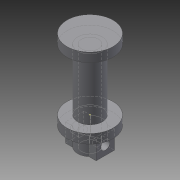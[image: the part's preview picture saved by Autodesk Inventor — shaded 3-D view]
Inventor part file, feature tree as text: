
AUTODESK INVENTOR PART (.ipt)
format: ipt  version: 2015 (Build 190159000, 159)  size: 158,208 bytes
history: native  units: mm
features: sketch x10, extrude x7, hole x2
ambient origin geometry x8: Origin, YZ Plane, XZ Plane, XY Plane, X Axis, Y Axis, Z Axis, Center Point
bodies: Solid1 (feature_tree)
feature tree (19):
  extrude  "Extrusion1"  Depth=5.5mm
  extrude  "Extrusion2"  Depth=20.0mm
  sketch  "Sketch3"  dims[d5=3.0mm d6=0.0mm d7=5.5mm]
  extrude  "Extrusion3"  Depth=5.5mm
  extrude  "Extrusion4"  Depth=3.0mm TaperAngle=0.0deg
  extrude  "Extrusion5"  Depth=3.0mm
  extrude  "Extrusion6"  Depth=6.0mm TaperAngle=0.0deg
  extrude  "Extrusion7"  Depth=20.0mm TaperAngle=0.0deg
  hole  "Hole1"  [1 undecoded]
  hole  "Hole2"  [1 undecoded]
  sketch  "Sketch1"  dims[d0=5.5mm d1=8.0mm]
  sketch  "Sketch2"  dims[d2=20.0mm d3=0.0mm d4=15.0mm]
  sketch  "Sketch4"  dims[d8=15.0mm d9=3.0mm d10=0.0mm]
  sketch  "Sketch5"  dims[d11=6.0mm d12=0.0mm d13=3.0mm]
  sketch  "Sketch6"  dims[d14=3.0mm d15=6.0mm d16=0.0mm]
  sketch  "Sketch7"  dims[d17=3.0mm d18=20.0mm d19=0.0mm]
  sketch  "Sketch8"  dims[d20=3.0mm d21=3.0mm]
  sketch  "Sketch9"  dims[d22=5.0mm d23=2.75mm]
  sketch  "Sketch10"  dims[d24=2.75mm d25=5.0mm d26=6.0mm d27=0.0mm d28=3.0mm d29=6.0mm d30=5.0mm d31=2.0mm d32=90.0deg d33=8.0mm d34=20.594885mm d35=3.0mm d36=6.0mm d37=5.0mm d38=2.0mm d39=90.0deg d40=8.0mm d41=20.594885mm]
note: 2 required parameter values undecoded (feature->parameter linkage not recoverable at this tier; creation-order binding heuristic only, values carry confidence <= 0.55)
